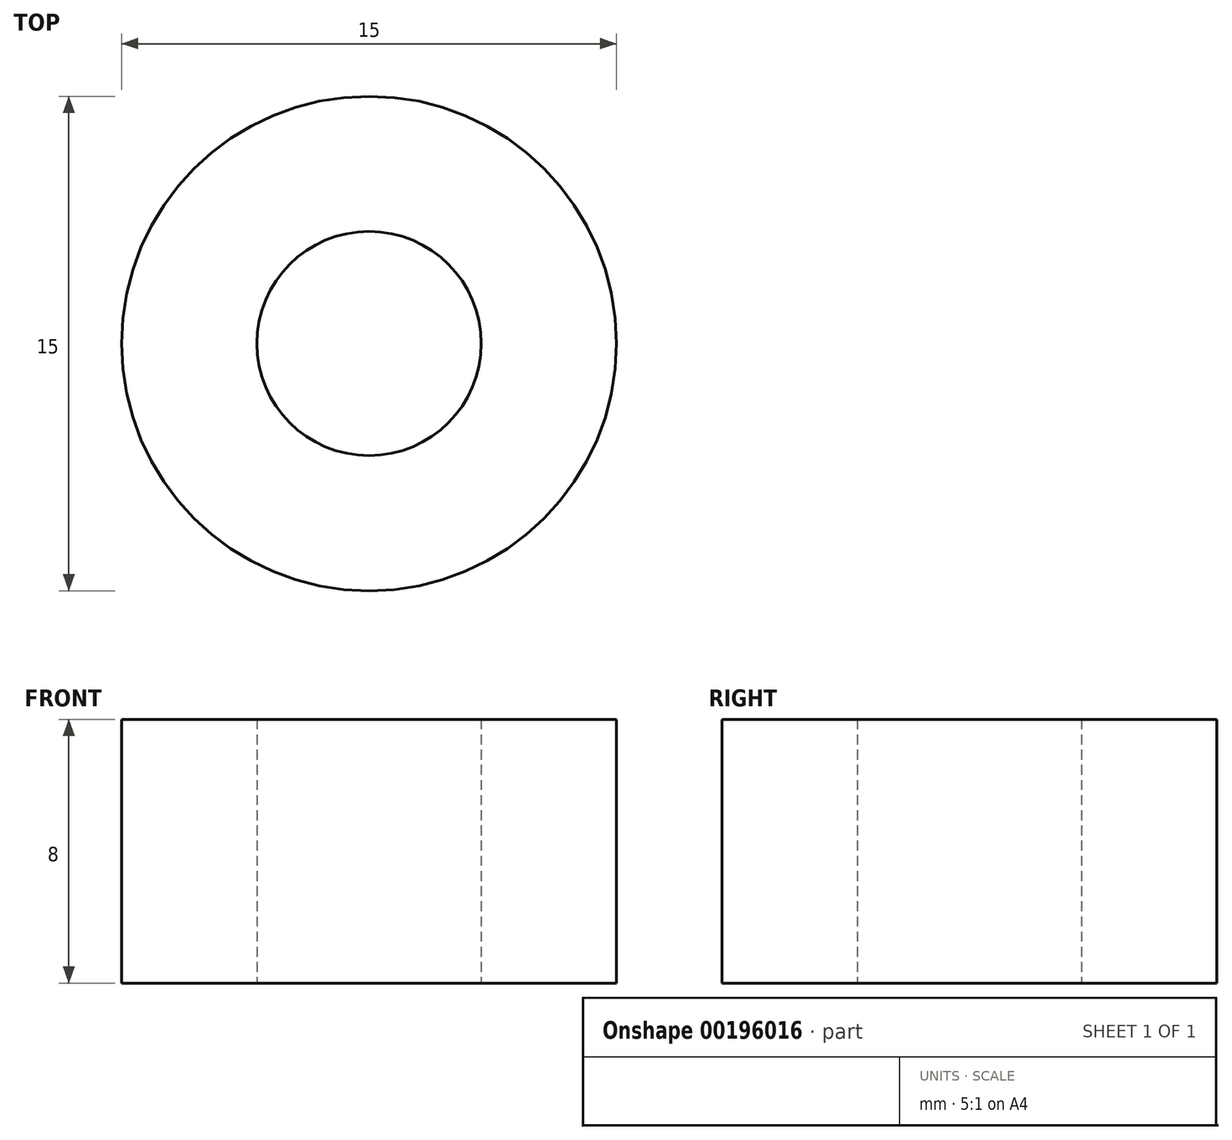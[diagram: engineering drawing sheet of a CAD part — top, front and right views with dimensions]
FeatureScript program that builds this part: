
annotation { "Feature Type Name" : "Feature", "Feature Type Description" : "" }
export const myFeature = defineFeature(function(context is Context, id is Id, definition is map)
    precondition{}
    {
        {
            var Q0;
            Q0=qCreatedBy(makeId("Top.planeOp"),FACE);
            var sketch = newSketch(context, id + "F0", { "sketchPlane" : qUnion([Q0])});
            skCircle(sketch, "E0", {"center": v(0, 0) * mm, "radius": 3.4 * mm});
            skCircle(sketch, "E1", {"center": v(0, 0) * mm, "radius": 7.5 * mm});
            skSolve(sketch);
        }
        {
            var Q0;
            Q0=makeQuery(id+"F0.imprint","IMPRINT",FACE,{"disambiguationData":[TD([[makeQuery(id+"F0.imprint","IMPRINT",EDGE,{"derivedFrom":sQuery(id+"F0.wireOp",EDGE,"E0")}),-1.0]])]});
            extrude(context, id + "F1", {"entities" : qUnion([Q0]), "depth" : 8 * mm});
        }
    });
